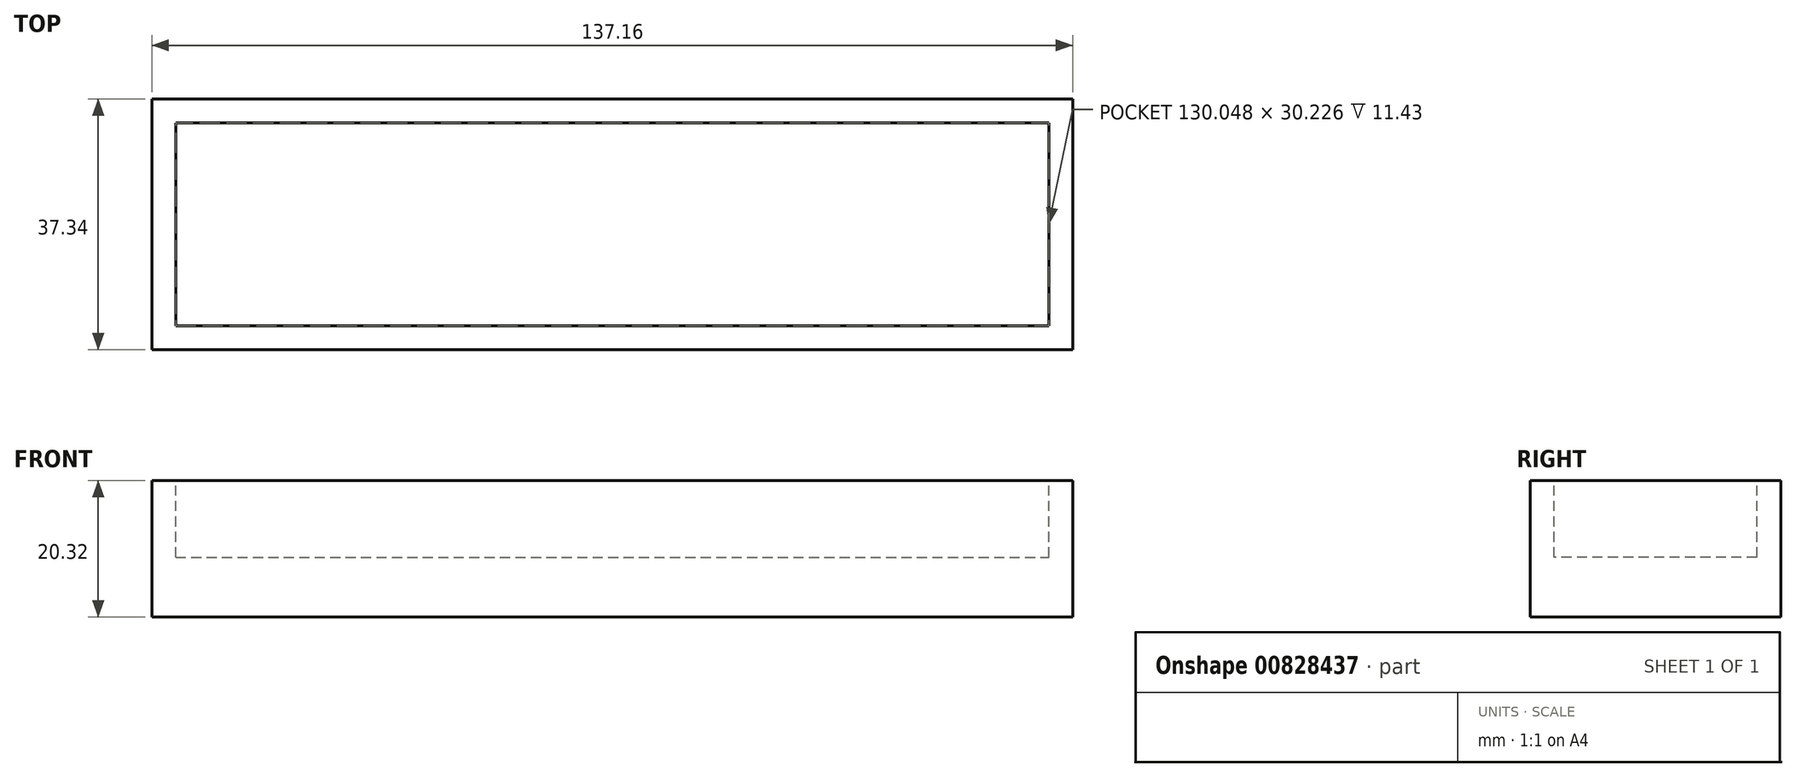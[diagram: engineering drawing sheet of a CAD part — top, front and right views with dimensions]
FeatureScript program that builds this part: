
annotation { "Feature Type Name" : "Feature", "Feature Type Description" : "" }
export const myFeature = defineFeature(function(context is Context, id is Id, definition is map)
    precondition{}
    {
        {
            var Q0;
            Q0=qCreatedBy(makeId("Top.planeOp"),FACE);
            var sketch = newSketch(context, id + "F0", { "sketchPlane" : qUnion([Q0])});
            skLineSegment(sketch, "E0.bottom", {"start": v(-68.58, 18.67) * mm, "end": v(68.58, 18.67) * mm});
            skLineSegment(sketch, "E0.top", {"start": v(-68.58, -18.67) * mm, "end": v(68.58, -18.67) * mm});
            skLineSegment(sketch, "E0.left", {"start": v(-68.58, 18.67) * mm, "end": v(-68.58, -18.67) * mm});
            skLineSegment(sketch, "E0.right", {"start": v(68.58, 18.67) * mm, "end": v(68.58, -18.67) * mm});
            skPoint(sketch, "E0.middle", {"position": v(0, 0) * mm});
            skSolve(sketch);
        }
        {
            var Q0;
            Q0=makeQuery(id+"F0.imprint","IMPRINT",FACE,{"disambiguationData":[TD([[makeQuery(id+"F0.imprint","IMPRINT",EDGE,{"derivedFrom":sQuery(id+"F0.wireOp",EDGE,"E0.bottom")}),-1.0]])]});
            extrude(context, id + "F1", {"entities" : qUnion([Q0]), "depth" : 20.32 * mm, "offsetDistance" : 25.4 * mm});
        }
        {
            var Q0;
            Q0=makeQuery(id+"F1.opExtrude","CAP_FACE",FACE,{"disambiguationData":[OSD([sQuery(id+"F0.wireOp",EDGE,"E0.bottom"),sQuery(id+"F0.wireOp",EDGE,"E0.top"),sQuery(id+"F0.wireOp",EDGE,"E0.left"),sQuery(id+"F0.wireOp",EDGE,"E0.right")])],"isStart":false});
            var sketch = newSketch(context, id + "F2", { "sketchPlane" : qUnion([Q0])});
            skLineSegment(sketch, "E1.bottom", {"start": v(-65.02, 15.11) * mm, "end": v(65.02, 15.11) * mm});
            skLineSegment(sketch, "E1.top", {"start": v(-65.02, -15.11) * mm, "end": v(65.02, -15.11) * mm});
            skLineSegment(sketch, "E1.left", {"start": v(-65.02, 15.11) * mm, "end": v(-65.02, -15.11) * mm});
            skLineSegment(sketch, "E1.right", {"start": v(65.02, 15.11) * mm, "end": v(65.02, -15.11) * mm});
            skPoint(sketch, "E1.middle", {"position": v(0, 0) * mm});
            skSolve(sketch);
        }
        {
            var Q0;
            Q0=qSketchRegion(id+"F2",true);
            extrude(context, id + "F3", {"entities" : qUnion([Q0]), "operationType" : NewBodyOperationType.REMOVE, "oppositeDirection" : true, "depth" : 11.43 * mm, "offsetDistance" : 25.4 * mm});
        }
    });
